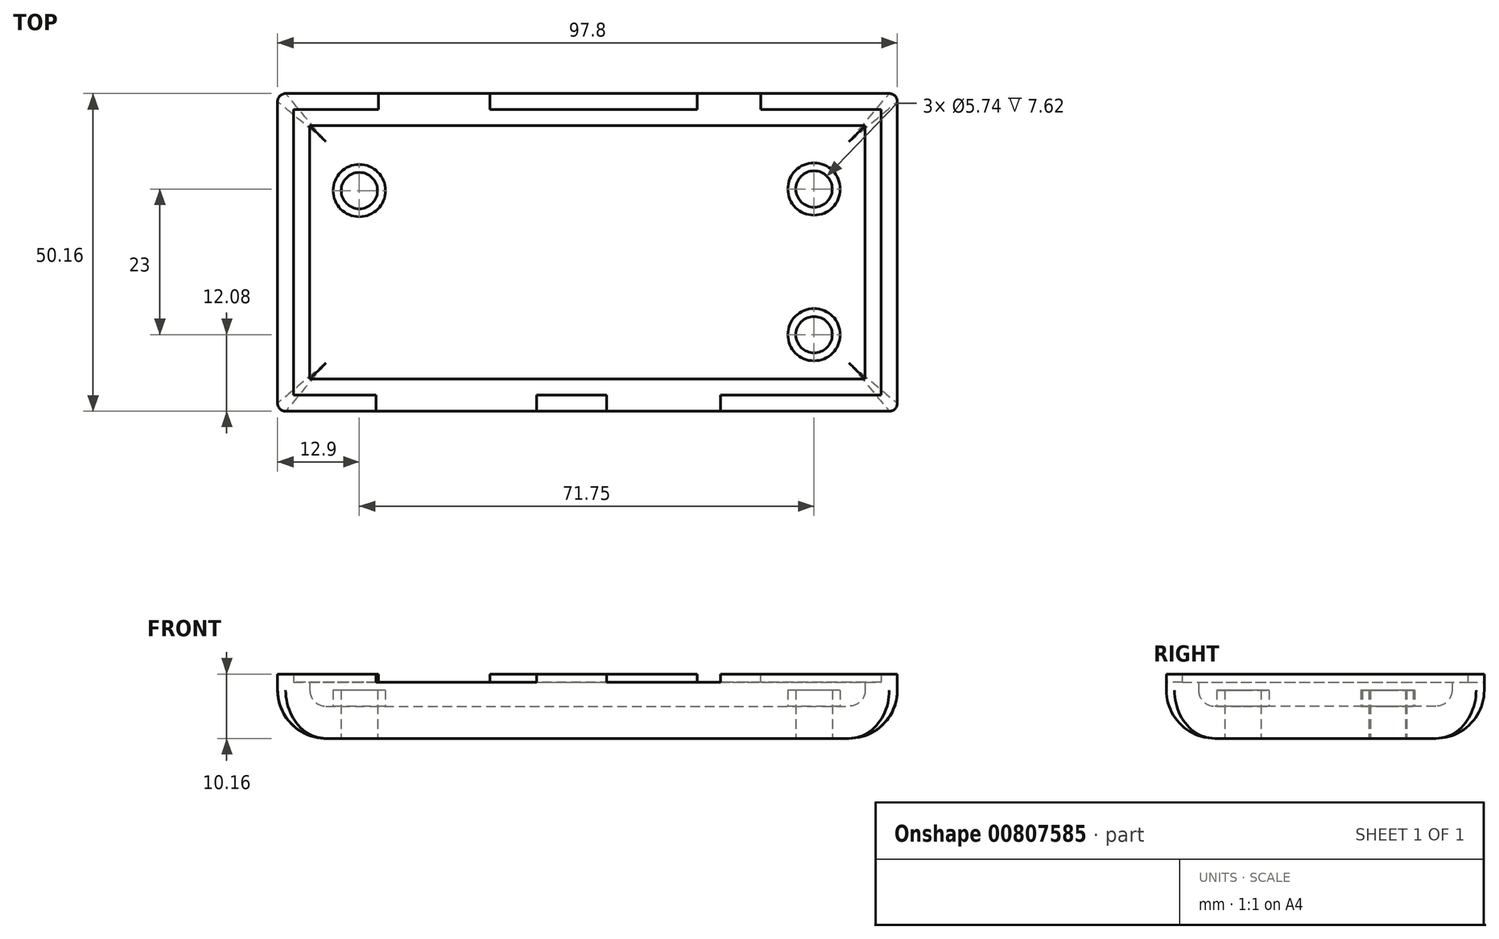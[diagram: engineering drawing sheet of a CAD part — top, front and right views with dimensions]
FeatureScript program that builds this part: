
annotation { "Feature Type Name" : "Feature", "Feature Type Description" : "" }
export const myFeature = defineFeature(function(context is Context, id is Id, definition is map)
    precondition{}
    {
        {
            var Q0;
            Q0=qCreatedBy(makeId("Top.planeOp"),FACE);
            var sketch = newSketch(context, id + "F0", { "sketchPlane" : qUnion([Q0])});
            skLineSegment(sketch, "E0.bottom", {"start": v(39, 16) * mm, "end": v(-39, 16) * mm, "construction": true});
            skLineSegment(sketch, "E0.top", {"start": v(39, -16) * mm, "end": v(-39, -16) * mm, "construction": true});
            skLineSegment(sketch, "E0.left", {"start": v(39, 16) * mm, "end": v(39, -16) * mm, "construction": true});
            skLineSegment(sketch, "E0.right", {"start": v(-39, 16) * mm, "end": v(-39, -16) * mm, "construction": true});
            skPoint(sketch, "E0.middle", {"position": v(0, 0) * mm});
            skCircle(sketch, "E1", {"center": v(-36, 9.75) * mm, "radius": 2.87 * mm});
            skCircle(sketch, "E2", {"center": v(35.75, 10) * mm, "radius": 2.87 * mm});
            skCircle(sketch, "E3", {"center": v(35.75, -13) * mm, "radius": 2.87 * mm});
            skLineSegment(sketch, "E4.bottom", {"start": v(-41.28, 17.46) * mm, "end": v(41.28, 17.46) * mm});
            skLineSegment(sketch, "E4.top", {"start": v(-41.28, -17.46) * mm, "end": v(41.28, -17.46) * mm});
            skLineSegment(sketch, "E4.left", {"start": v(-41.28, 17.46) * mm, "end": v(-41.28, -17.46) * mm});
            skLineSegment(sketch, "E4.right", {"start": v(41.28, 17.46) * mm, "end": v(41.28, -17.46) * mm});
            skSolve(sketch);
        }
        {
            var Q0;
            Q0 = qSketchRegion(id + "F0", true);
            extrude(context, id + "F1", {"entities" : qUnion([Q0]), "depth" : 5.08 * mm, "offsetDistance" : 25.4 * mm});
        }
        {
            var Q0;
            Q0=qCreatedBy(makeId("Front.planeOp"),FACE);
            var sketch = newSketch(context, id + "F2", { "sketchPlane" : qUnion([Q0])});
            skLineSegment(sketch, "E5.0", {"start": v(-41.28, 5.08) * mm, "end": v(-41.28, 0) * mm});
            skArc(sketch, "E6", {"start": v(-41.28, 5.08) * mm, "mid": v(-43.07, 5.82) * mm, "end": v(-43.82, 7.62) * mm});
            skArc(sketch, "E7", {"start": v(-41.28, 0) * mm, "mid": v(-46.66, 2.23) * mm, "end": v(-48.9, 7.62) * mm});
            skLineSegment(sketch, "E8", {"start": v(-48.9, 7.62) * mm, "end": v(-48.9, 10.16) * mm});
            skLineSegment(sketch, "E9", {"start": v(-48.9, 10.16) * mm, "end": v(-46.36, 10.16) * mm});
            skLineSegment(sketch, "E10", {"start": v(-46.36, 10.16) * mm, "end": v(-46.36, 8.9) * mm});
            skLineSegment(sketch, "E11", {"start": v(-46.36, 8.9) * mm, "end": v(-43.82, 8.9) * mm});
            skLineSegment(sketch, "E12", {"start": v(-43.82, 8.9) * mm, "end": v(-43.82, 7.62) * mm});
            skLineSegment(sketch, "E13", {"start": v(-48.9, 7.62) * mm, "end": v(-43.82, 7.62) * mm, "construction": true});
            skPoint(sketch, "E14", {"position": v(-46.36, 7.62) * mm});
            skSolve(sketch);
        }
        {
            var Q0;
            Q0 = qSketchRegion(id + "F2", true);
            var Q1;
            Q1=makeQuery(id+"F1.opExtrude","CAP_EDGE",EDGE,{"disambiguationData":[OSD([sQuery(id+"F0.wireOp",EDGE,"E4.left")])],"isStart":false});
            var Q2;
            Q2=makeQuery(id+"F1.opExtrude","CAP_EDGE",EDGE,{"disambiguationData":[OSD([sQuery(id+"F0.wireOp",EDGE,"E4.bottom")])],"isStart":false});
            var Q3;
            Q3=makeQuery(id+"F1.opExtrude","CAP_EDGE",EDGE,{"disambiguationData":[OSD([sQuery(id+"F0.wireOp",EDGE,"E4.right")])],"isStart":false});
            var Q4;
            Q4=makeQuery(id+"F1.opExtrude","CAP_EDGE",EDGE,{"disambiguationData":[OSD([sQuery(id+"F0.wireOp",EDGE,"E4.top")])],"isStart":false});
            sweep(context, id + "F3", {"operationType" : NewBodyOperationType.ADD, "profiles" : qUnion([Q0]), "path" : qUnion([Q1, Q2, Q3, Q4])});
        }
        {
            var Q0;
            Q0=makeQuery(id+"F3.opSweep","CAP_EDGE",EDGE,{"disambiguationData":[OSD([sQuery(id+"F0.wireOp",EDGE,"E4.top"),sQuery(id+"F0.wireOp",EDGE,"E4.left"),sQuery(id+"F2.wireOp",EDGE,"E7")])],"isStart":true});
            var Q1;
            Q1=makeQuery(id+"F3.opSweep","MID_CAP_EDGE",EDGE,{"disambiguationData":[OSD([sQuery(id+"F0.wireOp",EDGE,"E4.bottom"),sQuery(id+"F0.wireOp",EDGE,"E4.left"),sQuery(id+"F2.wireOp",EDGE,"E7")])],"capPos":3.0});
            var Q2;
            Q2=makeQuery(id+"F3.opSweep","MID_CAP_EDGE",EDGE,{"disambiguationData":[OSD([sQuery(id+"F0.wireOp",EDGE,"E4.bottom"),sQuery(id+"F0.wireOp",EDGE,"E4.right"),sQuery(id+"F2.wireOp",EDGE,"E7")])],"capPos":2.0});
            var Q3;
            Q3=makeQuery(id+"F3.opSweep","MID_CAP_EDGE",EDGE,{"disambiguationData":[OSD([sQuery(id+"F0.wireOp",EDGE,"E4.top"),sQuery(id+"F0.wireOp",EDGE,"E4.right"),sQuery(id+"F2.wireOp",EDGE,"E7")])],"capPos":1.0});
            fillet(context, id + "F4", {"entities" : qUnion([Q0, Q1, Q2, Q3]), "radius" : 1.27 * mm, "tangentPropagation" : true, "allowEdgeOverflow" : false});
        }
        {
            var Q0;
            Q0=makeQuery(id+"F3.opSweep","SWEPT_FACE",FACE,{"disambiguationData":[OSD([sQuery(id+"F0.wireOp",EDGE,"E4.bottom"),sQuery(id+"F2.wireOp",EDGE,"E8")])]});
            var sketch = newSketch(context, id + "F5", { "sketchPlane" : qUnion([Q0])});
            skLineSegment(sketch, "E15.bottom", {"start": v(15.4, 10.16) * mm, "end": v(33, 10.16) * mm});
            skLineSegment(sketch, "E15.top", {"start": v(15.4, 8.9) * mm, "end": v(33, 8.9) * mm});
            skLineSegment(sketch, "E15.left", {"start": v(15.4, 10.16) * mm, "end": v(15.4, 8.9) * mm});
            skLineSegment(sketch, "E15.right", {"start": v(33, 10.16) * mm, "end": v(33, 8.9) * mm});
            skPoint(sketch, "E16.0", {"position": v(39, 0) * mm});
            skPoint(sketch, "E17.0", {"position": v(-39, 0) * mm});
            skLineSegment(sketch, "E18.bottom", {"start": v(-27.33, 10.16) * mm, "end": v(-17.33, 10.16) * mm});
            skLineSegment(sketch, "E18.top", {"start": v(-27.33, 8.9) * mm, "end": v(-17.33, 8.9) * mm});
            skLineSegment(sketch, "E18.left", {"start": v(-27.33, 10.16) * mm, "end": v(-27.33, 8.9) * mm});
            skLineSegment(sketch, "E18.right", {"start": v(-17.33, 10.16) * mm, "end": v(-17.33, 8.9) * mm});
            skSolve(sketch);
        }
        {
            var Q0;
            Q0 = qSketchRegion(id + "F5", true);
            extrude(context, id + "F6", {"entities" : qUnion([Q0]), "operationType" : NewBodyOperationType.REMOVE, "oppositeDirection" : true, "depth" : 3.56 * mm, "offsetDistance" : 25.4 * mm});
        }
        {
            var Q0;
            Q0=makeQuery(id+"F1.opExtrude","CAP_FACE",FACE,{"disambiguationData":[OSD([sQuery(id+"F0.wireOp",EDGE,"E1"),sQuery(id+"F0.wireOp",EDGE,"E2"),sQuery(id+"F0.wireOp",EDGE,"E3"),sQuery(id+"F0.wireOp",EDGE,"E4.bottom"),sQuery(id+"F0.wireOp",EDGE,"E4.top"),sQuery(id+"F0.wireOp",EDGE,"E4.left"),sQuery(id+"F0.wireOp",EDGE,"E4.right")])],"isStart":false});
            var sketch = newSketch(context, id + "F7", { "sketchPlane" : qUnion([Q0])});
            skCircle(sketch, "E19", {"center": v(-36, 9.75) * mm, "radius": 4.13 * mm});
            skCircle(sketch, "E20", {"center": v(35.75, 10) * mm, "radius": 4.13 * mm});
            skCircle(sketch, "E21", {"center": v(35.75, -13) * mm, "radius": 4.13 * mm});
            skCircle(sketch, "E22.0", {"center": v(-36, 9.75) * mm, "radius": 2.87 * mm});
            skCircle(sketch, "E22.1", {"center": v(35.75, 10) * mm, "radius": 2.87 * mm});
            skCircle(sketch, "E22.2", {"center": v(35.75, -13) * mm, "radius": 2.87 * mm});
            skSolve(sketch);
        }
        {
            var Q0;
            Q0 = qSketchRegion(id + "F7", true);
            extrude(context, id + "F8", {"entities" : qUnion([Q0]), "operationType" : NewBodyOperationType.ADD, "depth" : 2.54 * mm, "offsetDistance" : 25.4 * mm});
        }
        {
            var Q0;
            Q0=makeQuery(id+"F3.opSweep","SWEPT_FACE",FACE,{"disambiguationData":[OSD([sQuery(id+"F0.wireOp",EDGE,"E4.top"),sQuery(id+"F2.wireOp",EDGE,"E8")])]});
            var sketch = newSketch(context, id + "F9", { "sketchPlane" : qUnion([Q0])});
            skPoint(sketch, "E23.0", {"position": v(-39, 0) * mm});
            skPoint(sketch, "E23.1", {"position": v(39, 0) * mm});
            skLineSegment(sketch, "E24.bottom", {"start": v(21, 10.16) * mm, "end": v(3, 10.16) * mm});
            skLineSegment(sketch, "E24.top", {"start": v(21, 8.9) * mm, "end": v(3, 8.89) * mm});
            skLineSegment(sketch, "E24.left", {"start": v(21, 10.16) * mm, "end": v(21, 8.89) * mm});
            skLineSegment(sketch, "E24.right", {"start": v(3, 10.16) * mm, "end": v(3, 8.89) * mm});
            skLineSegment(sketch, "E25.bottom", {"start": v(-33.37, 10.16) * mm, "end": v(-8.02, 10.16) * mm});
            skLineSegment(sketch, "E25.top", {"start": v(-33.37, 8.9) * mm, "end": v(-8.02, 8.9) * mm});
            skLineSegment(sketch, "E25.left", {"start": v(-33.37, 10.16) * mm, "end": v(-33.37, 8.9) * mm});
            skLineSegment(sketch, "E25.right", {"start": v(-8.02, 10.16) * mm, "end": v(-8.02, 8.9) * mm});
            skSolve(sketch);
        }
        {
            var Q0;
            Q0 = qSketchRegion(id + "F9", true);
            extrude(context, id + "F10", {"entities" : qUnion([Q0]), "operationType" : NewBodyOperationType.REMOVE, "oppositeDirection" : true, "depth" : 5.08 * mm, "offsetDistance" : 25.4 * mm});
        }
    });
